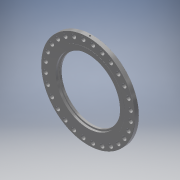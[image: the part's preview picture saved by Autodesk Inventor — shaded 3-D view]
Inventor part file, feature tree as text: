
AUTODESK INVENTOR PART (.ipt)
format: ipt  version: 2017.3 (Build 213257000, 257)  size: 310,784 bytes
history: native  units: in
note: dims shown in document units (in); Inventor stores cm internally (conversion verified against a paired STEP export)
features: sketch x6, extrude x4, chamfer x3, hole x2, pattern_circular x2, fillet x1, plane x1
ambient origin geometry x8: Origin, YZ Plane, XZ Plane, XY Plane, X Axis, Y Axis, Z Axis, Center Point
bodies: Solid1 (feature_tree)
feature tree (19):
  extrude  "Extrusion1"  Depth=1.906in TaperAngle=0.0deg
  extrude  "Extrusion2"  Depth=0.0625in TaperAngle=0.0deg
  extrude  "Extrusion3"  Depth=1.0in TaperAngle=0.0deg
  extrude  "Extrusion4"  Depth=2.0in TaperAngle=0.0deg
  hole  "Hole1"  [1 undecoded]
  chamfer  "Chamfer3"  Distance=11.0236in Angle=360.0deg
  pattern_circular  "Circular Pattern1"  Angle=45.0deg  [1 undecoded]
  chamfer  "Chamfer1"  Distance=0.0312in Angle=45.0deg
  chamfer  "Chamfer2"  Distance=0.0312in
  fillet  "Fillet2"  [1 undecoded]
  plane  "Work Plane1"
  hole  "Hole2"  [1 undecoded]
  pattern_circular  "Circular Pattern2"  [2 undecoded]
  sketch  "Sketch1"  dims[d0=43.0in d1=1.906in d2=0.0in]
  sketch  "Sketch2"  dims[d3=33.75in d4=0.0625in d5=0.0in]
  sketch  "Sketch3"  dims[d6=29.5in d7=1.0in d8=0.0in]
  sketch  "Sketch4"  dims[d9=28.0in d10=2.0in d11=0.0in]
  sketch  "Sketch5"  dims[d12=39.25in d13=0.0442in]
  sketch  "Sketch6"  dims[d14=1.875in d15=0.75in d16=0.375in d17=0.25in d18=0.5635in d19=1.0in d20=0.8108in d21=11.0236in d22=360.0deg d24=0.0625in d25=0.125in d26=45.0deg d28=0.0312in d29=0.125in d30=45.0deg d31=0.0312in d32=0.0in d33=0.0625in d34=0.125in d35=45.0deg d36=0.9688in d37=0.642in d38=2.0in d39=0.375in d40=0.25in d41=0.5635in d42=2.5in d43=0.8108in d44=0.7874in d45=360.0deg]
note: 6 required parameter values undecoded (feature->parameter linkage not recoverable at this tier; creation-order binding heuristic only, values carry confidence <= 0.55)
